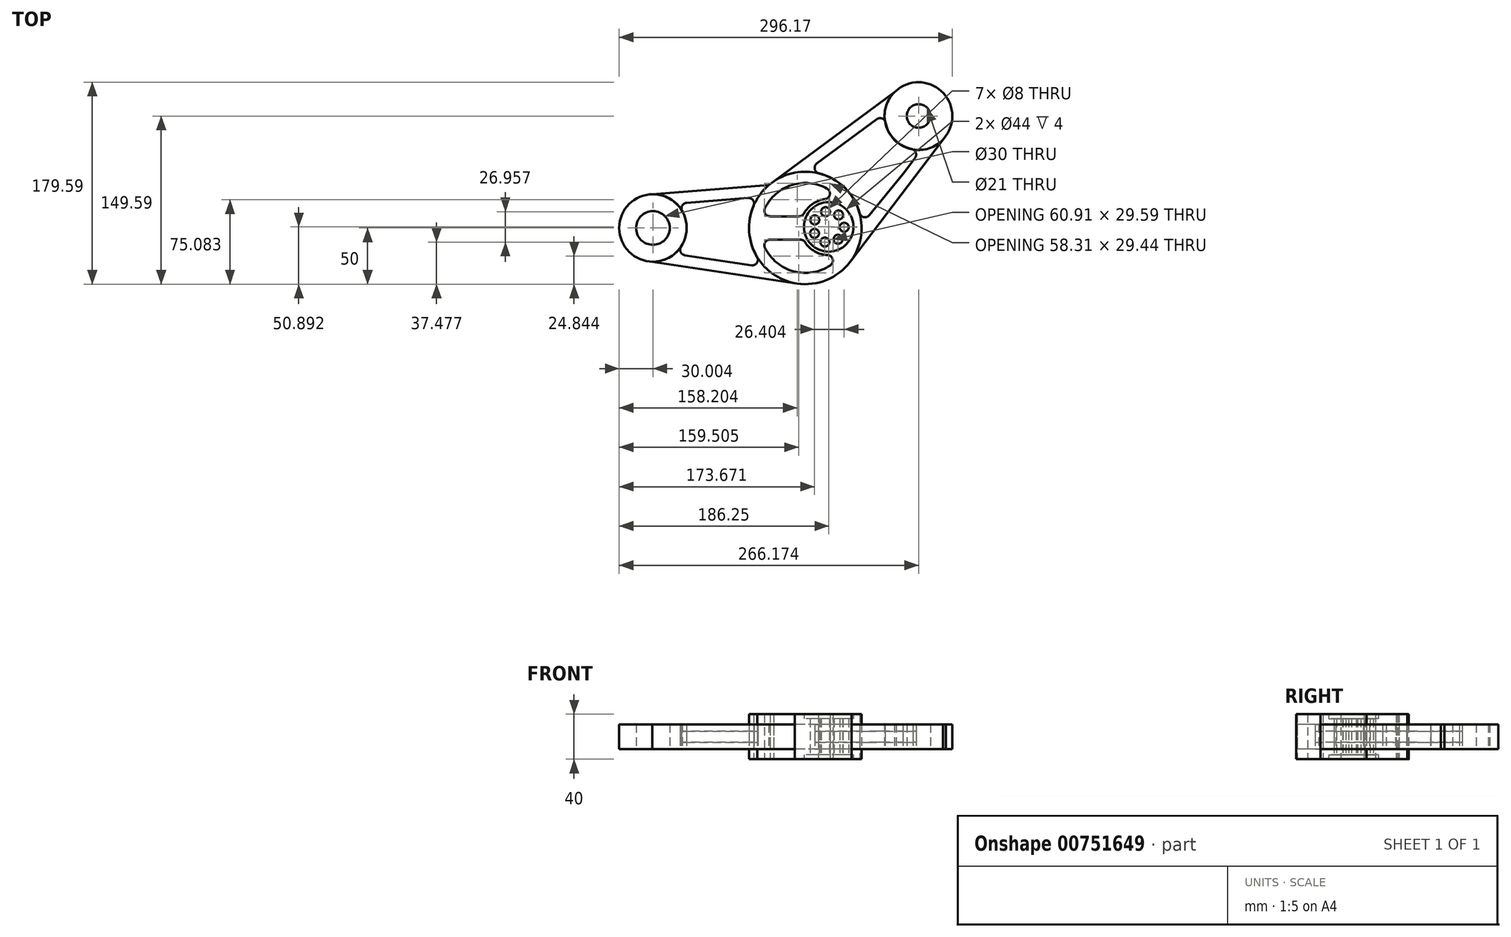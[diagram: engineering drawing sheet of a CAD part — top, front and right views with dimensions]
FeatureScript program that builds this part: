
annotation { "Feature Type Name" : "Feature", "Feature Type Description" : "" }
export const myFeature = defineFeature(function(context is Context, id is Id, definition is map)
    precondition{}
    {
        {
            var Q0;
            Q0=qCreatedBy(makeId("Top.planeOp"),FACE);
            var sketch = newSketch(context, id + "F0", { "sketchPlane" : qUnion([Q0])});
            skArc(sketch, "E0", {"start": v(-45.95, 19.7) * mm, "mid": v(-49.89, -3.36) * mm, "end": v(-42.9, -25.69) * mm});
            skArc(sketch, "E1", {"start": v(-35.94, -17.56) * mm, "mid": v(-10.4, -38.62) * mm, "end": v(22.26, -33.23) * mm});
            skCircle(sketch, "E2", {"center": v(20.76, 0.9) * mm, "radius": 22 * mm});
            skArc(sketch, "E3", {"start": v(-0.25, -12.65) * mm, "mid": v(8.33, -20.8) * mm, "end": v(19.7, -24.08) * mm});
            skCircle(sketch, "E4", {"center": v(29.6, 11.52) * mm, "radius": 4 * mm});
            skCircle(sketch, "E5.1.0", {"center": v(17.96, 14.43) * mm, "radius": 4 * mm});
            skCircle(sketch, "E5.2.0", {"center": v(8.43, 7.15) * mm, "radius": 4 * mm});
            skCircle(sketch, "E5.3.0", {"center": v(8.18, -4.85) * mm, "radius": 4 * mm});
            skCircle(sketch, "E5.4.0", {"center": v(17.4, -12.52) * mm, "radius": 4 * mm});
            skCircle(sketch, "E5.5.0", {"center": v(29.16, -10.1) * mm, "radius": 4 * mm});
            skCircle(sketch, "E5.6.0", {"center": v(34.59, 0.6) * mm, "radius": 4 * mm});
            skPoint(sketch, "E6.middle", {"position": v(-25.27, 0) * mm});
            skLineSegment(sketch, "E7.bottom", {"start": v(-5.52, 10.36) * mm, "end": v(-31.45, 10.36) * mm});
            skLineSegment(sketch, "E7.top", {"start": v(-4.46, -10.36) * mm, "end": v(-31.45, -10.36) * mm});
            skPoint(sketch, "E8.orphan", {"position": v(22.87, 10.36) * mm});
            skPoint(sketch, "E9.orphan", {"position": v(-26.95, -10.36) * mm});
            skPoint(sketch, "E7.right.end.orphan", {"position": v(-73.4, -10.36) * mm});
            skPoint(sketch, "E7.right.start.orphan", {"position": v(-23.59, 10.36) * mm});
            skPoint(sketch, "E10.visualSharp", {"position": v(-2.38, 10.36) * mm});
            skArc(sketch, "E10.filletArc", {"start": v(-5.52, 10.36) * mm, "mid": v(-2.98, 11.06) * mm, "end": v(-1.14, 12.95) * mm});
            skPoint(sketch, "E11.visualSharp", {"position": v(-38.63, 10.36) * mm});
            skArc(sketch, "E11.filletArc", {"start": v(-35.94, 17.56) * mm, "mid": v(-35.69, 12.71) * mm, "end": v(-31.45, 10.36) * mm});
            skPoint(sketch, "E12.visualSharp", {"position": v(-1.56, -10.36) * mm});
            skArc(sketch, "E12.filletArc", {"start": v(-0.25, -12.65) * mm, "mid": v(-2.06, -10.97) * mm, "end": v(-4.46, -10.36) * mm});
            skPoint(sketch, "E13.visualSharp", {"position": v(-38.63, -10.36) * mm});
            skArc(sketch, "E13.filletArc", {"start": v(-31.45, -10.36) * mm, "mid": v(-35.69, -12.71) * mm, "end": v(-35.94, -17.56) * mm});
            skArc(sketch, "E14.trimOffspring", {"start": v(17.55, 25.69) * mm, "mid": v(6.68, 21.55) * mm, "end": v(-1.14, 12.95) * mm});
            skArc(sketch, "E15.trimOffspring", {"start": v(19.33, 35.02) * mm, "mid": v(-12.05, 38.14) * mm, "end": v(-35.94, 17.56) * mm});
            skPoint(sketch, "E16.visualSharp", {"position": v(34.73, -19.84) * mm});
            skArc(sketch, "E16.filletArc", {"start": v(22.26, -33.23) * mm, "mid": v(24.3, -27.73) * mm, "end": v(19.7, -24.08) * mm});
            skPoint(sketch, "E17.visualSharp", {"position": v(32.9, 22.74) * mm});
            skArc(sketch, "E17.filletArc", {"start": v(17.55, 25.69) * mm, "mid": v(21.82, 29.71) * mm, "end": v(19.33, 35.02) * mm});
            skLineSegment(sketch, "E18", {"start": v(20.76, 0.9) * mm, "end": v(100.68, 99.59) * mm});
            skLineSegment(sketch, "E19", {"start": v(20.76, 0.9) * mm, "end": v(-135.49, 0) * mm});
            skArc(sketch, "E20", {"start": v(71.27, 93.67) * mm, "mid": v(79.39, 78.46) * mm, "end": v(94.54, 70.23) * mm});
            skCircle(sketch, "E21", {"center": v(100.68, 99.59) * mm, "radius": 10.5 * mm});
            skArc(sketch, "E22", {"start": v(-136.36, 29.99) * mm, "mid": v(-165.49, -0.22) * mm, "end": v(-135.93, -30) * mm});
            skCircle(sketch, "E23", {"center": v(-135.49, 0) * mm, "radius": 15 * mm});
            skLineSegment(sketch, "E24", {"start": v(80.68, 121.94) * mm, "end": v(-32.51, 38.14) * mm});
            skPoint(sketch, "E24.endSnap0", {"position": v(-12.05, 38.14) * mm});
            skLineSegment(sketch, "E25", {"start": v(124.85, 81.81) * mm, "end": v(39.83, -30.22) * mm});
            skLineSegment(sketch, "E26", {"start": v(-136.36, 29.99) * mm, "end": v(-32.51, 38.14) * mm});
            skLineSegment(sketch, "E27", {"start": v(-135.93, -30) * mm, "end": v(0, -50.57) * mm});
            skLineSegment(sketch, "E28", {"start": v(-93.37, 23.33) * mm, "end": v(-50.94, 26.66) * mm});
            skLineSegment(sketch, "E29", {"start": v(-93.37, 23.33) * mm, "end": v(-105.5, 22.38) * mm});
            skLineSegment(sketch, "E30", {"start": v(-81.27, -28.15) * mm, "end": v(-47.93, -33.2) * mm});
            skLineSegment(sketch, "E31", {"start": v(-81.27, -28.15) * mm, "end": v(-107.04, -24.25) * mm});
            skLineSegment(sketch, "E32", {"start": v(36.59, 76.86) * mm, "end": v(63.4, 96.7) * mm});
            skLineSegment(sketch, "E33", {"start": v(36.59, 76.86) * mm, "end": v(10.3, 57.4) * mm});
            skLineSegment(sketch, "E34", {"start": v(86.67, 48.05) * mm, "end": v(97.5, 62.3) * mm});
            skLineSegment(sketch, "E35", {"start": v(86.67, 48.05) * mm, "end": v(56.94, 11.34) * mm});
            skArc(sketch, "E36.trimOffspring", {"start": v(-110.47, -16.55) * mm, "mid": v(-105.5, -0.96) * mm, "end": v(-109.45, 14.9) * mm});
            skArc(sketch, "E37.trimOffspring", {"start": v(124.3, 81.1) * mm, "mid": v(121.19, 121.5) * mm, "end": v(80.68, 121.94) * mm});
            skPoint(sketch, "E38.visualSharp", {"position": v(-114.72, 21.66) * mm});
            skArc(sketch, "E38.filletArc", {"start": v(-105.5, 22.38) * mm, "mid": v(-109.54, 19.73) * mm, "end": v(-109.45, 14.9) * mm});
            skPoint(sketch, "E39.visualSharp", {"position": v(-116.09, -22.89) * mm});
            skArc(sketch, "E39.filletArc", {"start": v(-110.47, -16.55) * mm, "mid": v(-110.87, -21.34) * mm, "end": v(-107.04, -24.25) * mm});
            skPoint(sketch, "E40.visualSharp", {"position": v(70.8, 102.19) * mm});
            skArc(sketch, "E40.filletArc", {"start": v(71.27, 93.67) * mm, "mid": v(68.17, 97.35) * mm, "end": v(63.4, 96.7) * mm});
            skPoint(sketch, "E41.visualSharp", {"position": v(103.1, 69.69) * mm});
            skArc(sketch, "E41.filletArc", {"start": v(97.5, 62.3) * mm, "mid": v(98.2, 67.08) * mm, "end": v(94.54, 70.23) * mm});
            skArc(sketch, "E42.trimOffspring", {"start": v(48.24, 13.17) * mm, "mid": v(34.95, 35.76) * mm, "end": v(12.06, 48.52) * mm});
            skArc(sketch, "E43.trimOffspring", {"start": v(-7.48, -49.44) * mm, "mid": v(18.81, -46.33) * mm, "end": v(39.83, -30.22) * mm});
            skPoint(sketch, "E44.visualSharp", {"position": v(-41.84, 27.38) * mm});
            skArc(sketch, "E44.filletArc", {"start": v(-45.95, 19.7) * mm, "mid": v(-46.48, 24.6) * mm, "end": v(-50.94, 26.66) * mm});
            skPoint(sketch, "E45.visualSharp", {"position": v(-35.65, -35.06) * mm});
            skArc(sketch, "E45.filletArc", {"start": v(-47.93, -33.2) * mm, "mid": v(-43.03, -31.04) * mm, "end": v(-42.9, -25.69) * mm});
            skPoint(sketch, "E46.visualSharp", {"position": v(0.3, 50) * mm});
            skArc(sketch, "E46.filletArc", {"start": v(10.3, 57.4) * mm, "mid": v(8.37, 52.4) * mm, "end": v(12.06, 48.52) * mm});
            skPoint(sketch, "E47.visualSharp", {"position": v(49.93, 2.67) * mm});
            skArc(sketch, "E47.filletArc", {"start": v(48.24, 13.17) * mm, "mid": v(52.03, 9.59) * mm, "end": v(56.94, 11.34) * mm});
            skCircle(sketch, "E48", {"center": v(-135.49, 0) * mm, "radius": 30 * mm});
            skCircle(sketch, "E49", {"center": v(0, 0) * mm, "radius": 50.04 * mm});
            skCircle(sketch, "E50", {"center": v(100.68, 99.59) * mm, "radius": 30.23 * mm});
            skSolve(sketch);
        }
        {
            var Q0;
            Q0=makeQuery(id+"F0.imprint","IMPRINT",FACE,{"disambiguationData":[TD([[makeQuery(id+"F0.imprint","IMPRINT",EDGE,{"derivedFrom":sQuery(id+"F0.wireOp",EDGE,"E1")}),-1.0]])]});
            var Q1;
            Q1=makeQuery(id+"F0.imprint","IMPRINT",FACE,{"disambiguationData":[TD([[makeQuery(id+"F0.imprint","IMPRINT",EDGE,{"derivedFrom":sQuery(id+"F0.wireOp",EDGE,"E7.bottom")}),1.0]])]});
            extrude(context, id + "F1", {"entities" : qUnion([Q0, Q1]), "endBound" : BoundingType.SYMMETRIC, "depth" : 40 * mm, "offsetDistance" : 25 * mm});
        }
        {
            var Q0;
            Q0=makeQuery(id+"F0.imprint","IMPRINT",FACE,{"disambiguationData":[TD([[makeQuery(id+"F0.imprint","IMPRINT",EDGE,{"derivedFrom":sQuery(id+"F0.wireOp",EDGE,"E23")}),-1.0]])]});
            extrude(context, id + "F2", {"entities" : qUnion([Q0]), "endBound" : BoundingType.SYMMETRIC, "depth" : 22 * mm, "offsetDistance" : 25 * mm});
        }
        {
            var Q0;
            Q0=makeQuery(id+"F0.imprint","IMPRINT",FACE,{"disambiguationData":[TD([[makeQuery(id+"F0.imprint","IMPRINT",EDGE,{"derivedFrom":sQuery(id+"F0.wireOp",EDGE,"E21")}),-1.0]])]});
            extrude(context, id + "F3", {"entities" : qUnion([Q0]), "endBound" : BoundingType.SYMMETRIC, "depth" : 22 * mm, "offsetDistance" : 25 * mm});
        }
        {
            var Q0;
            Q0=makeQuery(id+"F0.imprint","IMPRINT",FACE,{"disambiguationData":[TD([[makeQuery(id+"F0.imprint","IMPRINT",EDGE,{"derivedFrom":sQuery(id+"F0.wireOp",EDGE,"E5.1.0")}),-1.0]])]});
            var Q1;
            Q1=makeQuery(id+"F0.imprint","IMPRINT",FACE,{"disambiguationData":[TD([[makeQuery(id+"F0.imprint","IMPRINT",EDGE,{"derivedFrom":sQuery(id+"F0.wireOp",EDGE,"E5.3.0")}),-1.0]])]});
            extrude(context, id + "F4", {"entities" : qUnion([Q0, Q1]), "operationType" : NewBodyOperationType.ADD, "endBound" : BoundingType.SYMMETRIC, "depth" : 32 * mm, "offsetDistance" : 25 * mm});
        }
        {
            var Q0;
            {var subQ1=sQuery(id+"F0.wireOp",EDGE,"E26");Q0=makeQuery(id+"F0.imprint","IMPRINT",FACE,{"disambiguationData":[TD([[makeQuery(id+"F0.imprint","IMPRINT",EDGE,{"derivedFrom":subQ1}),-1.0]])]});}
            var Q1;
            {var subQ1=sQuery(id+"F0.wireOp",EDGE,"E30");Q1=makeQuery(id+"F0.imprint","IMPRINT",FACE,{"disambiguationData":[TD([[makeQuery(id+"F0.imprint","IMPRINT",EDGE,{"derivedFrom":subQ1}),-1.0]])]});}
            var Q2;
            {var subQ1=sQuery(id+"F0.wireOp",EDGE,"E34");Q2=makeQuery(id+"F0.imprint","IMPRINT",FACE,{"disambiguationData":[TD([[makeQuery(id+"F0.imprint","IMPRINT",EDGE,{"derivedFrom":subQ1}),-1.0]])]});}
            var Q3;
            {var subQ1=sQuery(id+"F0.wireOp",EDGE,"E32");Q3=makeQuery(id+"F0.imprint","IMPRINT",FACE,{"disambiguationData":[TD([[makeQuery(id+"F0.imprint","IMPRINT",EDGE,{"derivedFrom":subQ1}),1.0]])]});}
            extrude(context, id + "F5", {"entities" : qUnion([Q0, Q1, Q2, Q3]), "endBound" : BoundingType.SYMMETRIC, "depth" : 22 * mm, "offsetDistance" : 25 * mm});
        }
        {
            var Q0;
            {var subQ1=sQuery(id+"F0.wireOp",EDGE,"E28");Q0=makeQuery(id+"F0.imprint","IMPRINT",FACE,{"disambiguationData":[TD([[makeQuery(id+"F0.imprint","IMPRINT",EDGE,{"derivedFrom":subQ1}),-1.0]])]});}
            var Q1;
            {var subQ1=sQuery(id+"F0.wireOp",EDGE,"E30");Q1=makeQuery(id+"F0.imprint","IMPRINT",FACE,{"disambiguationData":[TD([[makeQuery(id+"F0.imprint","IMPRINT",EDGE,{"derivedFrom":subQ1}),1.0]])]});}
            var Q2;
            {var subQ1=sQuery(id+"F0.wireOp",EDGE,"E32");Q2=makeQuery(id+"F0.imprint","IMPRINT",FACE,{"disambiguationData":[TD([[makeQuery(id+"F0.imprint","IMPRINT",EDGE,{"derivedFrom":subQ1}),-1.0]])]});}
            var Q3;
            {var subQ1=sQuery(id+"F0.wireOp",EDGE,"E34");Q3=makeQuery(id+"F0.imprint","IMPRINT",FACE,{"disambiguationData":[TD([[makeQuery(id+"F0.imprint","IMPRINT",EDGE,{"derivedFrom":subQ1}),1.0]])]});}
            extrude(context, id + "F6", {"entities" : qUnion([Q0, Q1, Q2, Q3]), "endBound" : BoundingType.SYMMETRIC, "depth" : 10 * mm, "offsetDistance" : 25 * mm});
        }
    });
